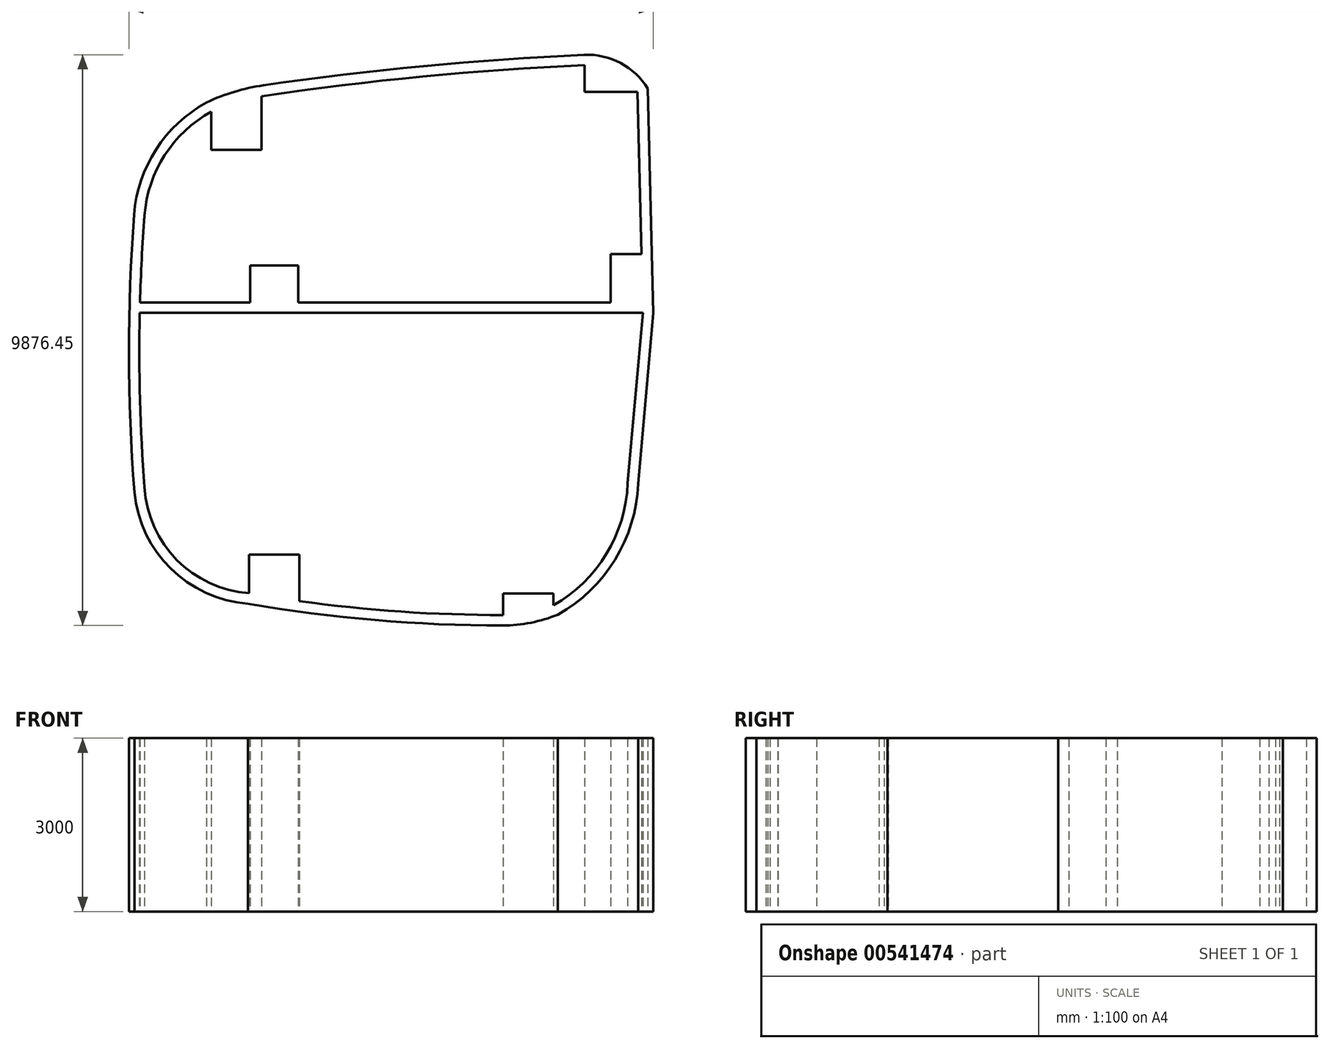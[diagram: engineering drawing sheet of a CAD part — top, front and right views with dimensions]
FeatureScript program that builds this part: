
annotation { "Feature Type Name" : "Feature", "Feature Type Description" : "" }
export const myFeature = defineFeature(function(context is Context, id is Id, definition is map)
    precondition{}
    {
        {
            var Q0;
            Q0=qCreatedBy(makeId("Top.planeOp"),FACE);
            var sketch = newSketch(context, id + "F0", { "sketchPlane" : qUnion([Q0])});
            skLineSegment(sketch, "E0.0", {"start": v(-3080.54, 4395.05) * mm, "end": v(-3080.54, 5051.72) * mm});
            skLineSegment(sketch, "E1.0", {"start": v(-2210.54, 4395.05) * mm, "end": v(-3080.54, 4395.05) * mm});
            skLineSegment(sketch, "E2.0", {"start": v(-2210.54, 5321.5) * mm, "end": v(-2210.54, 4395.05) * mm});
            skLineSegment(sketch, "E3.0", {"start": v(3374.46, 5857.48) * mm, "end": v(3374.46, 5395.05) * mm});
            skLineSegment(sketch, "E4.0", {"start": v(3374.46, 5395.05) * mm, "end": v(4292.48, 5395.05) * mm});
            skLineSegment(sketch, "E5.0", {"start": v(4359.93, 2590.05) * mm, "end": v(3824.46, 2590.05) * mm});
            skLineSegment(sketch, "E6.0", {"start": v(3824.46, 2590.05) * mm, "end": v(3824.46, 1748.05) * mm});
            skLineSegment(sketch, "E7.0", {"start": v(-1575.54, 1748.05) * mm, "end": v(-1575.54, 2390.05) * mm});
            skLineSegment(sketch, "E8.0", {"start": v(-1575.54, 2390.05) * mm, "end": v(-2405.54, 2390.05) * mm});
            skLineSegment(sketch, "E9.0", {"start": v(-2405.54, 2390.05) * mm, "end": v(-2405.54, 1748.05) * mm});
            skLineSegment(sketch, "E10.0", {"start": v(-2425.54, -2609.95) * mm, "end": v(-2425.54, -3281) * mm});
            skLineSegment(sketch, "E11.0", {"start": v(-1555.54, -2609.95) * mm, "end": v(-2425.54, -2609.95) * mm});
            skLineSegment(sketch, "E12.0", {"start": v(-1555.54, -3417.15) * mm, "end": v(-1555.54, -2609.95) * mm});
            skLineSegment(sketch, "E13.0", {"start": v(1964.46, -3284.95) * mm, "end": v(1964.46, -3657.9) * mm});
            skLineSegment(sketch, "E14.0", {"start": v(2834.46, -3284.95) * mm, "end": v(1964.46, -3284.95) * mm});
            skLineSegment(sketch, "E15.0", {"start": v(2834.46, -3488.8) * mm, "end": v(2834.46, -3284.95) * mm});
            skLineSegment(sketch, "E16.0", {"start": v(-4317.16, 1570.05) * mm, "end": v(4384.46, 1570.05) * mm});
            skPoint(sketch, "E17.0", {"position": v(4122.36, -1373.96) * mm});
            skArc(sketch, "E18", {"start": v(2834.46, -3488.8) * mm, "mid": v(3754.18, -2599.32) * mm, "end": v(4122.36, -1373.96) * mm});
            skLineSegment(sketch, "E19", {"start": v(4122.36, -1373.96) * mm, "end": v(4384.46, 1570.05) * mm});
            skLineSegment(sketch, "E20", {"start": v(4384.46, 1570.05) * mm, "end": v(4292.48, 5395.05) * mm});
            skArc(sketch, "E21", {"start": v(4292.48, 5395.05) * mm, "mid": v(3893.93, 5746.29) * mm, "end": v(3374.46, 5857.48) * mm});
            skArc(sketch, "E22", {"start": v(3374.46, 5857.48) * mm, "mid": v(575.16, 5660.43) * mm, "end": v(-2210.54, 5321.5) * mm});
            skPoint(sketch, "E23.0", {"position": v(-4236.13, 3256.61) * mm});
            skArc(sketch, "E24", {"start": v(-3080.54, 5051.72) * mm, "mid": v(-3886.12, 4300.8) * mm, "end": v(-4236.13, 3256.61) * mm});
            skArc(sketch, "E25", {"start": v(-4236.13, 3256.61) * mm, "mid": v(-4324.2, 905.4) * mm, "end": v(-4236.13, -1445.8) * mm});
            skArc(sketch, "E26", {"start": v(-4236.13, -1445.8) * mm, "mid": v(-3676.49, -2704.42) * mm, "end": v(-2425.54, -3281) * mm});
            skArc(sketch, "E27", {"start": v(-2425.54, -3281) * mm, "mid": v(-238.73, -3564.93) * mm, "end": v(1964.46, -3657.9) * mm});
            skArc(sketch, "E28", {"start": v(1964.46, -3657.9) * mm, "mid": v(2407.55, -3614.94) * mm, "end": v(2834.46, -3488.8) * mm});
            skArc(sketch, "E29", {"start": v(-2210.54, 5321.5) * mm, "mid": v(-2655.37, 5218.32) * mm, "end": v(-3080.54, 5051.72) * mm});
            skArc(sketch, "E30.0", {"start": v(-4410.19, -1530.67) * mm, "mid": v(-3781.5, -2853.92) * mm, "end": v(-2447.67, -3459.86) * mm});
            skArc(sketch, "E30.1", {"start": v(-4415.62, 3270.08) * mm, "mid": v(-4504.17, 869.6) * mm, "end": v(-4410.19, -1530.67) * mm});
            skArc(sketch, "E30.2", {"start": v(-3162.7, 5211.95) * mm, "mid": v(-4036.11, 4400.35) * mm, "end": v(-4415.62, 3270.08) * mm});
            skArc(sketch, "E30.3", {"start": v(-2178.41, 5508.16) * mm, "mid": v(-2682.09, 5398.37) * mm, "end": v(-3162.7, 5211.95) * mm});
            skArc(sketch, "E30.4", {"start": v(3366.39, 6037.3) * mm, "mid": v(587.34, 5842.41) * mm, "end": v(-2178.41, 5508.16) * mm});
            skArc(sketch, "E30.5", {"start": v(-2447.67, -3459.86) * mm, "mid": v(-249.7, -3744.65) * mm, "end": v(1964.7, -3837.9) * mm});
            skArc(sketch, "E30.6", {"start": v(1964.7, -3837.9) * mm, "mid": v(2447.69, -3790.5) * mm, "end": v(2912.62, -3651.35) * mm});
            skArc(sketch, "E30.7", {"start": v(2912.62, -3651.35) * mm, "mid": v(3903.6, -2700) * mm, "end": v(4302.06, -1385.34) * mm});
            skLineSegment(sketch, "E30.8", {"start": v(4302.06, -1385.34) * mm, "end": v(4564.65, 1564.21) * mm});
            skLineSegment(sketch, "E30.9", {"start": v(4564.65, 1564.21) * mm, "end": v(4471.21, 5449.72) * mm});
            skArc(sketch, "E30.10", {"start": v(4471.21, 5449.72) * mm, "mid": v(3999.1, 5894.52) * mm, "end": v(3366.39, 6037.3) * mm});
            skLineSegment(sketch, "E31", {"start": v(-4312.9, 1748.05) * mm, "end": v(4380.18, 1748.05) * mm});
            skSolve(sketch);
        }
        {
            var Q0;
            Q0 = qSketchRegion(id + "F0", true);
            var Q1;
            Q1=makeQuery(id+"F0.imprint","IMPRINT",FACE,{"disambiguationData":[TD([[makeQuery(id+"F0.imprint","IMPRINT",EDGE,{"derivedFrom":sQuery(id+"F0.wireOp",EDGE,"E0.0")}),-1.0]])]});
            var Q2;
            Q2=makeQuery(id+"F0.imprint","IMPRINT",FACE,{"disambiguationData":[TD([[makeQuery(id+"F0.imprint","IMPRINT",EDGE,{"derivedFrom":sQuery(id+"F0.wireOp",EDGE,"E3.0")}),1.0]])]});
            var Q3;
            {var subQ4=sQuery(id+"F0.wireOp",EDGE,"E16.0");Q3=makeQuery(id+"F0.imprint","IMPRINT",FACE,{"disambiguationData":[TD([[makeQuery(id+"F0.imprint","IMPRINT",EDGE,{"derivedFrom":subQ4}),1.0]])]});}
            var Q4;
            {var subQ0=sQuery(id+"F0.wireOp",EDGE,"E7.0");Q4=makeQuery(id+"F0.imprint","IMPRINT",FACE,{"disambiguationData":[TD([[makeQuery(id+"F0.imprint","IMPRINT",EDGE,{"derivedFrom":subQ0}),1.0]])]});}
            var Q5;
            {var subQ0=sQuery(id+"F0.wireOp",EDGE,"E5.0");Q5=makeQuery(id+"F0.imprint","IMPRINT",FACE,{"disambiguationData":[TD([[makeQuery(id+"F0.imprint","IMPRINT",EDGE,{"derivedFrom":subQ0}),1.0]])]});}
            var Q6;
            {var subQ0=sQuery(id+"F0.wireOp",EDGE,"E10.0");Q6=makeQuery(id+"F0.imprint","IMPRINT",FACE,{"disambiguationData":[TD([[makeQuery(id+"F0.imprint","IMPRINT",EDGE,{"derivedFrom":subQ0}),1.0]])]});}
            var Q7;
            Q7=makeQuery(id+"F0.imprint","IMPRINT",FACE,{"disambiguationData":[TD([[makeQuery(id+"F0.imprint","IMPRINT",EDGE,{"derivedFrom":sQuery(id+"F0.wireOp",EDGE,"E13.0")}),1.0]])]});
            extrude(context, id + "F1", {"entities" : qUnion([Q0, Q1, Q2, Q3, Q4, Q5, Q6, Q7]), "depth" : 3000 * mm, "offsetDistance" : 25 * mm});
        }
    });
